# Revit family: BE Coil
name_source: partatom
category: Pipe Accessories
units: mm (PartAtom-declared; Revit-internal decimal feet)

## family parameters
Always vertical = Yes
Cut with Voids When Loaded = No
Part Type = Normal
Round Connector Dimension = Use Diameter
Shared = Yes
Work Plane-Based = No

## types (5) — shared parameters
Coil connection = Connection Box
Enclosure rating = IP67
IfcExportAs = IfcValveType
IfcExportType = BE
Manufacturer = Danfoss
URL = https://www.danfoss.com

## per-type parameters (varying)
| type | Ambient temperature range | Description | Frequency | Model | Power consumption | Supply voltage a.c. | Supply voltage d.c. |
| BE230AS 220-230V 50Hz Box_018F6701 | -40 - 80 °C | BE024AS 24V 50Hz Box | 50 Hz | 018F6707 | 10 W | 220-230 V | - |
| BE024AS 24V 50Hz Box_018F6707 | -40 - 80 °C | BE230AS 220-230V 50Hz Box | 50 Hz | 018F6701 | 10 W | 24 V | - |
| BE240CS 208-240V 50/60Hz Low Power_018F6783 | -25 - 55 °C | BE230AS 220-230V 50Hz Box | 50/60 Hz | 018F6783 | 4 W | 208 - 240 V | - |
| BE012DS 12V DC Box_018F6796 | -40 - 50 °C | BE012DS 12V DC Box | - | 018F6796 | 15,0 W | - | 12,00 V |
| BE024DS 24V DC Box_018F6797 | -40 - 50 °C | BE024DS 24V DC Box | - | 018F6797 | 16,0 W | - | 24,00 V |

## geometry (parser evidence)
native form markers: Sweep x2
no freeform markers — native parametric forms only
